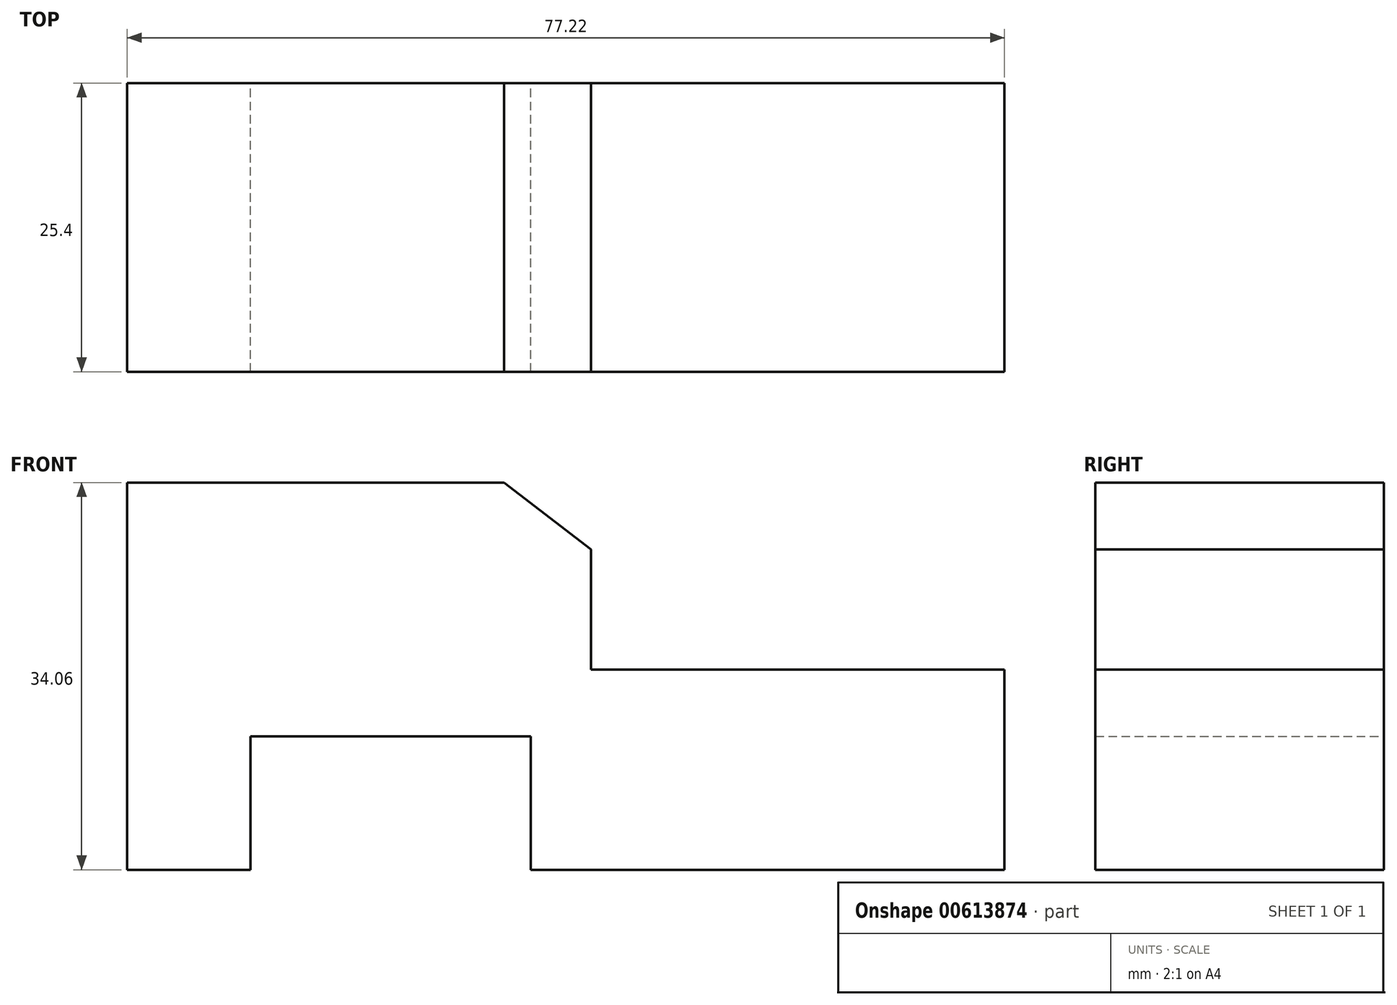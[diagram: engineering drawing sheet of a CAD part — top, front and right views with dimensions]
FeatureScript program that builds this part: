
annotation { "Feature Type Name" : "Feature", "Feature Type Description" : "" }
export const myFeature = defineFeature(function(context is Context, id is Id, definition is map)
    precondition{}
    {
        {
            var Q0;
            Q0=qCreatedBy(makeId("Front.planeOp"),FACE);
            var sketch = newSketch(context, id + "F0", { "sketchPlane" : qUnion([Q0])});
            skLineSegment(sketch, "E0", {"start": v(-72.08, 37.29) * mm, "end": v(-38.9, 37.29) * mm});
            skLineSegment(sketch, "E1", {"start": v(-38.9, 37.29) * mm, "end": v(-31.27, 31.42) * mm});
            skLineSegment(sketch, "E2", {"start": v(-31.27, 31.42) * mm, "end": v(-31.27, 20.85) * mm});
            skLineSegment(sketch, "E3", {"start": v(-31.27, 20.85) * mm, "end": v(5.14, 20.85) * mm});
            skLineSegment(sketch, "E4", {"start": v(5.14, 20.85) * mm, "end": v(5.14, 3.23) * mm});
            skLineSegment(sketch, "E5", {"start": v(5.14, 3.23) * mm, "end": v(-36.56, 3.23) * mm});
            skLineSegment(sketch, "E6", {"start": v(-36.56, 3.23) * mm, "end": v(-36.56, 14.97) * mm});
            skLineSegment(sketch, "E7", {"start": v(-36.56, 14.97) * mm, "end": v(-61.22, 14.97) * mm});
            skLineSegment(sketch, "E8", {"start": v(-61.22, 14.97) * mm, "end": v(-61.22, 3.23) * mm});
            skLineSegment(sketch, "E9", {"start": v(-61.22, 3.23) * mm, "end": v(-72.08, 3.23) * mm});
            skLineSegment(sketch, "E10", {"start": v(-72.08, 3.23) * mm, "end": v(-72.08, 37.29) * mm});
            skSolve(sketch);
        }
        {
            var Q0;
            Q0 = qSketchRegion(id + "F0", true);
            extrude(context, id + "F1", {"entities" : qUnion([Q0]), "depth" : 25.4 * mm, "offsetDistance" : 25.4 * mm});
        }
    });
